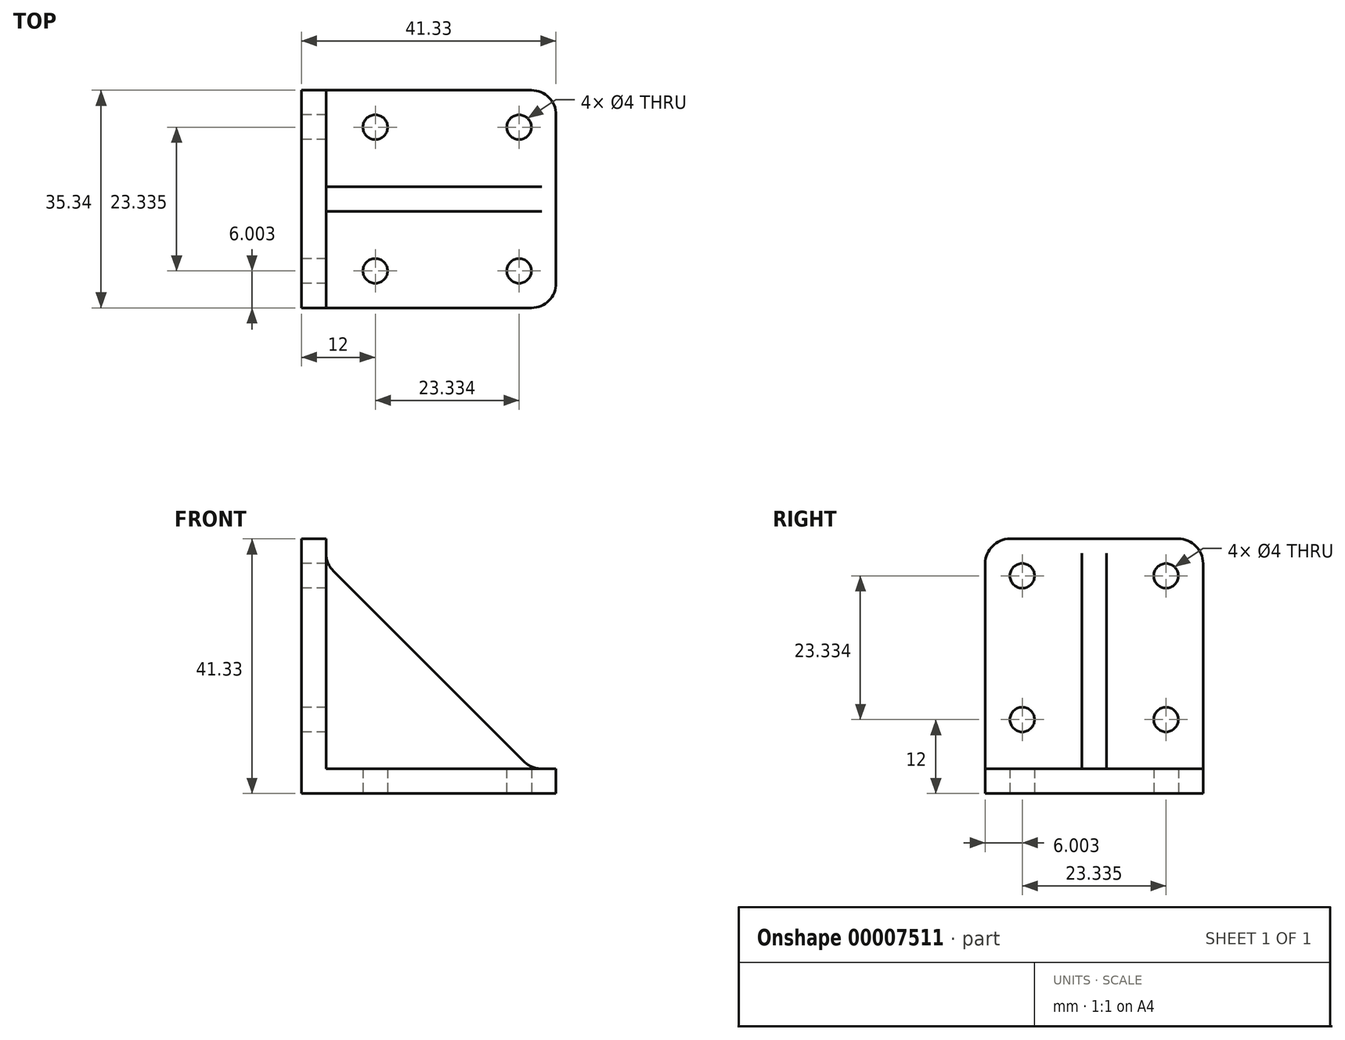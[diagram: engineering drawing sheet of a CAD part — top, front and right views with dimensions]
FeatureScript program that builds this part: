
annotation { "Feature Type Name" : "Feature", "Feature Type Description" : "" }
export const myFeature = defineFeature(function(context is Context, id is Id, definition is map)
    precondition{}
    {
        {
            var Q0;
            Q0=qCreatedBy(makeId("Top.planeOp"),FACE);
            var sketch = newSketch(context, id + "F0", { "sketchPlane" : qUnion([Q0])});
            skCircle(sketch, "E0", {"center": v(12, 11.67) * mm, "radius": 2 * mm});
            skCircle(sketch, "E1", {"center": v(35.33, 11.67) * mm, "radius": 2 * mm});
            skCircle(sketch, "E2", {"center": v(35.33, -11.67) * mm, "radius": 2 * mm});
            skCircle(sketch, "E3", {"center": v(12, -11.67) * mm, "radius": 2 * mm});
            skLineSegment(sketch, "E4", {"start": v(12, -11.67) * mm, "end": v(35.33, 11.67) * mm, "construction": true});
            skLineSegment(sketch, "E5", {"start": v(35.33, -11.67) * mm, "end": v(12, 11.67) * mm, "construction": true});
            skLineSegment(sketch, "E6", {"start": v(12, 11.67) * mm, "end": v(35.33, 11.67) * mm, "construction": true});
            skLineSegment(sketch, "E7", {"start": v(35.33, -11.67) * mm, "end": v(12, -11.67) * mm, "construction": true});
            skLineSegment(sketch, "E8", {"start": v(12, 11.67) * mm, "end": v(12, -11.67) * mm, "construction": true});
            skLineSegment(sketch, "E9", {"start": v(35.33, 11.67) * mm, "end": v(35.33, -11.67) * mm, "construction": true});
            skLineSegment(sketch, "E10.0", {"start": v(0, 17.67) * mm, "end": v(0, -17.67) * mm});
            skLineSegment(sketch, "E10.1", {"start": v(0, 17.67) * mm, "end": v(41.33, 17.67) * mm});
            skLineSegment(sketch, "E10.2", {"start": v(41.33, 17.67) * mm, "end": v(41.33, -17.67) * mm});
            skLineSegment(sketch, "E10.3", {"start": v(41.33, -17.67) * mm, "end": v(0, -17.67) * mm});
            skLineSegment(sketch, "E11", {"start": v(12, -11.67) * mm, "end": v(12, -17.67) * mm, "construction": true});
            skLineSegment(sketch, "E12", {"start": v(12, -11.67) * mm, "end": v(0, -11.67) * mm, "construction": true});
            skLineSegment(sketch, "E13", {"start": v(12, 11.67) * mm, "end": v(12, 17.67) * mm, "construction": true});
            skLineSegment(sketch, "E14", {"start": v(35.33, 11.67) * mm, "end": v(35.33, 17.67) * mm, "construction": true});
            skLineSegment(sketch, "E15", {"start": v(35.33, 11.67) * mm, "end": v(41.33, 11.67) * mm, "construction": true});
            skLineSegment(sketch, "E16", {"start": v(35.33, -11.67) * mm, "end": v(41.33, -11.67) * mm, "construction": true});
            skLineSegment(sketch, "E17", {"start": v(35.33, -11.67) * mm, "end": v(35.33, -17.67) * mm, "construction": true});
            skSolve(sketch);
        }
        {
            var Q0;
            Q0=qCreatedBy(makeId("Right.planeOp"),FACE);
            var sketch = newSketch(context, id + "F1", { "sketchPlane" : qUnion([Q0])});
            skPoint(sketch, "E18.0", {"position": v(-11.67, 0) * mm});
            skPoint(sketch, "E18.1", {"position": v(11.67, 0) * mm});
            skLineSegment(sketch, "E19", {"start": v(-11.67, 0) * mm, "end": v(-11.67, 12) * mm, "construction": true});
            skCircle(sketch, "E20", {"center": v(-11.67, 12) * mm, "radius": 2 * mm});
            skLineSegment(sketch, "E21", {"start": v(11.67, 0) * mm, "end": v(11.67, 12) * mm, "construction": true});
            skCircle(sketch, "E22", {"center": v(11.67, 12) * mm, "radius": 2 * mm});
            skCircle(sketch, "E23", {"center": v(-11.67, 35.33) * mm, "radius": 2 * mm});
            skCircle(sketch, "E24", {"center": v(11.67, 35.33) * mm, "radius": 2 * mm});
            skLineSegment(sketch, "E25", {"start": v(11.67, 12) * mm, "end": v(-11.67, 35.33) * mm, "construction": true});
            skLineSegment(sketch, "E26", {"start": v(-11.67, 12) * mm, "end": v(11.67, 35.33) * mm, "construction": true});
            skLineSegment(sketch, "E27", {"start": v(-11.67, 12) * mm, "end": v(11.67, 12) * mm, "construction": true});
            skLineSegment(sketch, "E28", {"start": v(11.67, 12) * mm, "end": v(11.67, 35.33) * mm, "construction": true});
            skLineSegment(sketch, "E29", {"start": v(11.67, 35.33) * mm, "end": v(-11.67, 35.33) * mm, "construction": true});
            skPoint(sketch, "E30.0", {"position": v(-17.67, 0) * mm});
            skPoint(sketch, "E30.1", {"position": v(17.67, 0) * mm});
            skLineSegment(sketch, "E31", {"start": v(17.67, 0) * mm, "end": v(-17.67, 0) * mm});
            skLineSegment(sketch, "E32", {"start": v(-17.67, 0) * mm, "end": v(-17.67, 41.33) * mm});
            skLineSegment(sketch, "E33", {"start": v(-17.67, 41.33) * mm, "end": v(17.67, 41.33) * mm});
            skLineSegment(sketch, "E34", {"start": v(17.67, 41.33) * mm, "end": v(17.67, 0) * mm});
            skLineSegment(sketch, "E35", {"start": v(-11.67, 35.33) * mm, "end": v(-11.67, 41.33) * mm, "construction": true});
            skSolve(sketch);
        }
        {
            var Q0;
            Q0=qCreatedBy(makeId("Front.planeOp"),FACE);
            var sketch = newSketch(context, id + "F2", { "sketchPlane" : qUnion([Q0])});
            skLineSegment(sketch, "E36", {"start": v(41.33, 0) * mm, "end": v(0, 41.33) * mm});
            skLineSegment(sketch, "E37", {"start": v(0, 41.33) * mm, "end": v(0, 0) * mm});
            skLineSegment(sketch, "E38", {"start": v(0, 0) * mm, "end": v(41.33, 0) * mm});
            skPoint(sketch, "E39.0", {"position": v(0, 41.33) * mm});
            skSolve(sketch);
        }
        {
            var Q0;
            Q0=makeQuery(id+"F0.imprint","IMPRINT",FACE,{"disambiguationData":[TD([[makeQuery(id+"F0.imprint","IMPRINT",EDGE,{"derivedFrom":sQuery(id+"F0.wireOp",EDGE,"E0")}),-1.0]])]});
            extrude(context, id + "F3", {"entities" : qUnion([Q0]), "depth" : 4 * mm});
        }
        {
            var Q0;
            Q0=makeQuery(id+"F1.imprint","IMPRINT",FACE,{"disambiguationData":[TD([[makeQuery(id+"F1.imprint","IMPRINT",EDGE,{"derivedFrom":sQuery(id+"F1.wireOp",EDGE,"E20")}),-1.0]])]});
            extrude(context, id + "F4", {"entities" : qUnion([Q0]), "operationType" : NewBodyOperationType.ADD, "depth" : 4 * mm});
        }
        {
            var Q0;
            Q0=makeQuery(id+"F2.imprint","IMPRINT",FACE,{"disambiguationData":[TD([[makeQuery(id+"F2.imprint","IMPRINT",EDGE,{"derivedFrom":sQuery(id+"F2.wireOp",EDGE,"E36")}),1.0]])]});
            extrude(context, id + "F5", {"entities" : qUnion([Q0]), "operationType" : NewBodyOperationType.ADD, "endBound" : BoundingType.SYMMETRIC, "depth" : 4 * mm});
        }
        {
            var Q0;
            {var subQ0=sQuery(id+"F0.wireOp",EDGE,"E10.3");var subQ1=makeQuery(id+"F3.opExtrude","CAP_FACE",FACE,{"disambiguationData":[OSD([sQuery(id+"F0.wireOp",EDGE,"E0"),sQuery(id+"F0.wireOp",EDGE,"E1"),sQuery(id+"F0.wireOp",EDGE,"E2"),sQuery(id+"F0.wireOp",EDGE,"E3"),sQuery(id+"F0.wireOp",EDGE,"E10.0"),sQuery(id+"F0.wireOp",EDGE,"E10.1"),sQuery(id+"F0.wireOp",EDGE,"E10.2"),subQ0])],"isStart":false});var subQ2=sQuery(id+"F1.wireOp",EDGE,"3de330b1-310b-46dd-a1ee-5d6f6d7bf4e0");var subQ3=makeQuery(id+"F4.opExtrude","CAP_FACE",FACE,{"disambiguationData":[OSD([subQ2,sQuery(id+"F1.wireOp",EDGE,"43beb749-815b-4d92-85b9-475490c45cec"),sQuery(id+"F1.wireOp",EDGE,"77a5d65a-ee38-47b7-9e75-6fb28c5271e5"),sQuery(id+"F1.wireOp",EDGE,"49d745fc-9574-497a-8d8c-6e1d91027d8f"),sQuery(id+"F1.wireOp",EDGE,"467ef579-36df-4ecf-8d20-890fd8efc65f"),sQuery(id+"F1.wireOp",EDGE,"cd0c1a65-d245-4723-ac41-a15121c7cf7e"),sQuery(id+"F1.wireOp",EDGE,"2ae26674-83a6-4553-bd60-26fc024872ea"),sQuery(id+"F1.wireOp",EDGE,"da967565-b174-4d6f-85f2-eeaf1e1e553d")])],"isStart":false});Q0=makeQuery(id+"F5.boolean.opBoolean","SPLIT",EDGE,{"disambiguationData":[TD([makeQuery(id+"F3.opExtrude","SWEPT_FACE",FACE,{"disambiguationData":[OSD([subQ0])]})])],"derivedFrom":makeQuery(id+"F4.boolean.opBoolean","INTERSECT",EDGE,{"derivedFrom":[subQ1,subQ3]})});}
            var Q1;
            {var subQ0=sQuery(id+"F0.wireOp",EDGE,"E10.1");var subQ1=makeQuery(id+"F3.opExtrude","CAP_FACE",FACE,{"disambiguationData":[OSD([sQuery(id+"F0.wireOp",EDGE,"E0"),sQuery(id+"F0.wireOp",EDGE,"E1"),sQuery(id+"F0.wireOp",EDGE,"E2"),sQuery(id+"F0.wireOp",EDGE,"E3"),sQuery(id+"F0.wireOp",EDGE,"E10.0"),subQ0,sQuery(id+"F0.wireOp",EDGE,"E10.2"),sQuery(id+"F0.wireOp",EDGE,"E10.3")])],"isStart":false});var subQ2=sQuery(id+"F1.wireOp",EDGE,"77a5d65a-ee38-47b7-9e75-6fb28c5271e5");var subQ3=makeQuery(id+"F4.opExtrude","CAP_FACE",FACE,{"disambiguationData":[OSD([sQuery(id+"F1.wireOp",EDGE,"3de330b1-310b-46dd-a1ee-5d6f6d7bf4e0"),sQuery(id+"F1.wireOp",EDGE,"43beb749-815b-4d92-85b9-475490c45cec"),subQ2,sQuery(id+"F1.wireOp",EDGE,"49d745fc-9574-497a-8d8c-6e1d91027d8f"),sQuery(id+"F1.wireOp",EDGE,"467ef579-36df-4ecf-8d20-890fd8efc65f"),sQuery(id+"F1.wireOp",EDGE,"cd0c1a65-d245-4723-ac41-a15121c7cf7e"),sQuery(id+"F1.wireOp",EDGE,"2ae26674-83a6-4553-bd60-26fc024872ea"),sQuery(id+"F1.wireOp",EDGE,"da967565-b174-4d6f-85f2-eeaf1e1e553d")])],"isStart":false});Q1=makeQuery(id+"F5.boolean.opBoolean","SPLIT",EDGE,{"disambiguationData":[TD([makeQuery(id+"F3.opExtrude","SWEPT_FACE",FACE,{"disambiguationData":[OSD([subQ0])]})])],"derivedFrom":makeQuery(id+"F4.boolean.opBoolean","INTERSECT",EDGE,{"derivedFrom":[subQ1,subQ3]})});}
            var Q2;
            Q2=makeQuery(id+"F3.opExtrude","SWEPT_EDGE",EDGE,{"disambiguationData":[OSD([sQuery(id+"F0.wireOp",EDGE,"E10.2"),sQuery(id+"F0.wireOp",EDGE,"E10.3")])]});
            var Q3;
            Q3=makeQuery(id+"F3.opExtrude","SWEPT_EDGE",EDGE,{"disambiguationData":[OSD([sQuery(id+"F0.wireOp",EDGE,"E10.1"),sQuery(id+"F0.wireOp",EDGE,"E10.2")])]});
            var Q4;
            Q4=makeQuery(id+"F4.opExtrude","SWEPT_EDGE",EDGE,{"disambiguationData":[OSD([sQuery(id+"F1.wireOp",EDGE,"3de330b1-310b-46dd-a1ee-5d6f6d7bf4e0"),sQuery(id+"F1.wireOp",EDGE,"43beb749-815b-4d92-85b9-475490c45cec")])]});
            var Q5;
            Q5=makeQuery(id+"F4.opExtrude","SWEPT_EDGE",EDGE,{"disambiguationData":[OSD([sQuery(id+"F1.wireOp",EDGE,"43beb749-815b-4d92-85b9-475490c45cec"),sQuery(id+"F1.wireOp",EDGE,"77a5d65a-ee38-47b7-9e75-6fb28c5271e5")])]});
            var Q6;
            Q6=makeQuery(id+"F4.opExtrude","SWEPT_EDGE",EDGE,{"disambiguationData":[OSD([sQuery(id+"F1.wireOp",EDGE,"E32"),sQuery(id+"F1.wireOp",EDGE,"E33")])]});
            var Q7;
            Q7=makeQuery(id+"F4.opExtrude","SWEPT_EDGE",EDGE,{"disambiguationData":[OSD([sQuery(id+"F1.wireOp",EDGE,"E33"),sQuery(id+"F1.wireOp",EDGE,"E34")])]});
            var Q8;
            Q8=makeQuery(id+"F5.boolean.opBoolean","INTERSECT",EDGE,{"derivedFrom":[makeQuery(id+"F4.opExtrude","CAP_FACE",FACE,{"disambiguationData":[OSD([sQuery(id+"F1.wireOp",EDGE,"E20"),sQuery(id+"F1.wireOp",EDGE,"E22"),sQuery(id+"F1.wireOp",EDGE,"E23"),sQuery(id+"F1.wireOp",EDGE,"E24"),sQuery(id+"F1.wireOp",EDGE,"E31"),sQuery(id+"F1.wireOp",EDGE,"E32"),sQuery(id+"F1.wireOp",EDGE,"E33"),sQuery(id+"F1.wireOp",EDGE,"E34")])],"isStart":false}),makeQuery(id+"F5.opExtrude","SWEPT_FACE",FACE,{"disambiguationData":[OSD([sQuery(id+"F2.wireOp",EDGE,"E36")])]})]});
            var Q9;
            Q9=makeQuery(id+"F5.boolean.opBoolean","INTERSECT",EDGE,{"derivedFrom":[makeQuery(id+"F3.opExtrude","CAP_FACE",FACE,{"disambiguationData":[OSD([sQuery(id+"F0.wireOp",EDGE,"E0"),sQuery(id+"F0.wireOp",EDGE,"E1"),sQuery(id+"F0.wireOp",EDGE,"E2"),sQuery(id+"F0.wireOp",EDGE,"E3"),sQuery(id+"F0.wireOp",EDGE,"E10.0"),sQuery(id+"F0.wireOp",EDGE,"E10.1"),sQuery(id+"F0.wireOp",EDGE,"E10.2"),sQuery(id+"F0.wireOp",EDGE,"E10.3")])],"isStart":false}),makeQuery(id+"F5.opExtrude","SWEPT_FACE",FACE,{"disambiguationData":[OSD([sQuery(id+"F2.wireOp",EDGE,"E36")])]})]});
            fillet(context, id + "F6", {"entities" : qUnion([Q0, Q1, Q2, Q3, Q4, Q5, Q6, Q7, Q8, Q9]), "radius" : 4 * mm, "tangentPropagation" : true, "allowEdgeOverflow" : false});
        }
    });
